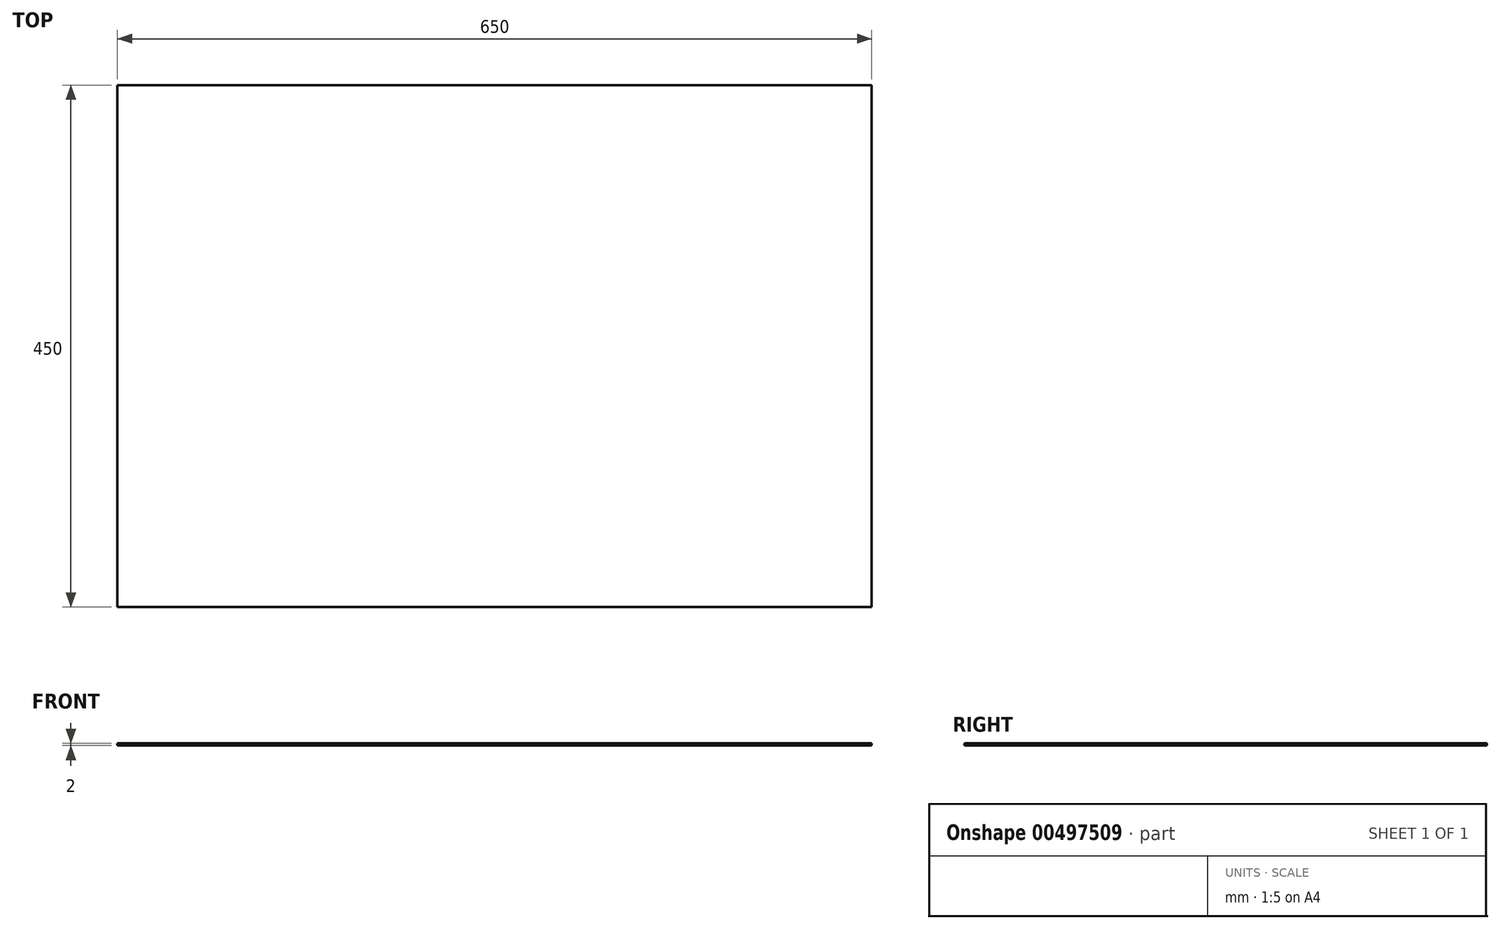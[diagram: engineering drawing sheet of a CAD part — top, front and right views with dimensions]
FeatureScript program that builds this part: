
annotation { "Feature Type Name" : "Feature", "Feature Type Description" : "" }
export const myFeature = defineFeature(function(context is Context, id is Id, definition is map)
    precondition{}
    {
        {
            var Q0;
            Q0=qCreatedBy(makeId("Top.planeOp"),FACE);
            var sketch = newSketch(context, id + "F0", { "sketchPlane" : qUnion([Q0])});
            skLineSegment(sketch, "E0.bottom", {"start": v(-335.77, 237.12) * mm, "end": v(314.23, 237.12) * mm});
            skLineSegment(sketch, "E0.top", {"start": v(-335.77, -212.88) * mm, "end": v(314.23, -212.88) * mm});
            skLineSegment(sketch, "E0.left", {"start": v(-335.77, 237.12) * mm, "end": v(-335.77, -212.88) * mm});
            skLineSegment(sketch, "E0.right", {"start": v(314.23, 237.12) * mm, "end": v(314.23, -212.88) * mm});
            skSolve(sketch);
        }
        {
            var Q0;
            Q0 = qSketchRegion(id + "F0", true);
            extrude(context, id + "F1", {"entities" : qUnion([Q0]), "depth" : 2 * mm, "offsetDistance" : 25 * mm});
        }
    });
